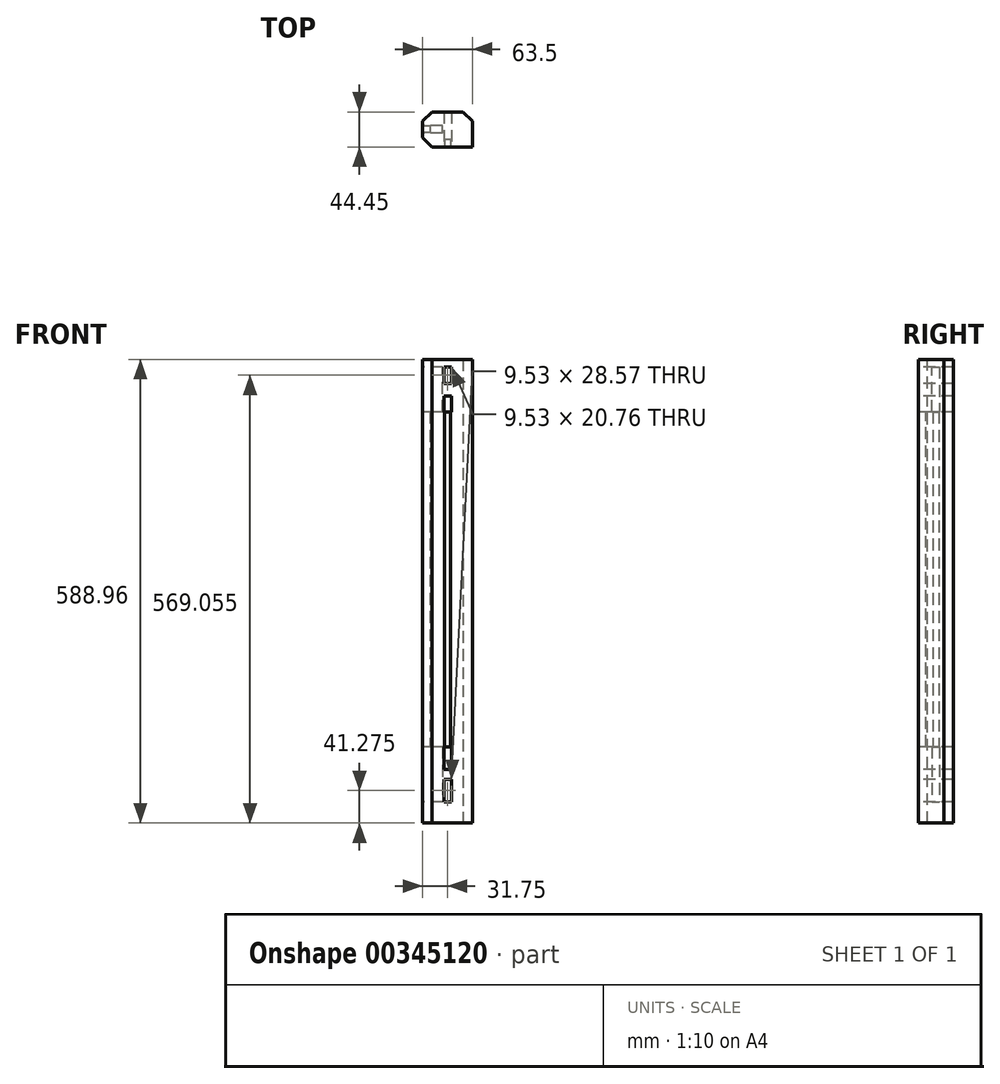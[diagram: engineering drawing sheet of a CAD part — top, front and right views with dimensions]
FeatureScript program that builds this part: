
annotation { "Feature Type Name" : "Feature", "Feature Type Description" : "" }
export const myFeature = defineFeature(function(context is Context, id is Id, definition is map)
    precondition{}
    {
        {
            var Q0;
            Q0=qCreatedBy(makeId("Top.planeOp"),FACE);
            var sketch = newSketch(context, id + "F0", { "sketchPlane" : qUnion([Q0])});
            skLineSegment(sketch, "E0", {"start": v(0, 0) * mm, "end": v(63.5, 0) * mm});
            skLineSegment(sketch, "E1", {"start": v(63.5, 0) * mm, "end": v(63.5, 44.45) * mm});
            skLineSegment(sketch, "E2", {"start": v(63.5, 44.45) * mm, "end": v(0, 44.45) * mm});
            skLineSegment(sketch, "E3", {"start": v(0, 44.45) * mm, "end": v(0, 0) * mm});
            skSolve(sketch);
        }
        {
            var Q0;
            Q0=qSketchRegion(id+"F0",true);
            extrude(context, id + "F1", {"entities" : qUnion([Q0]), "depth" : 588.96 * mm});
        }
        {
            var Q0;
            Q0=makeQuery(id+"F1.opExtrude","SWEPT_FACE",FACE,{"disambiguationData":[OSD([sQuery(id+"F0.wireOp",EDGE,"E3")])]});
            var sketch = newSketch(context, id + "F2", { "sketchPlane" : qUnion([Q0])});
            skLineSegment(sketch, "E4", {"start": v(-26.99, 579.44) * mm, "end": v(-26.99, 522.29) * mm});
            skLineSegment(sketch, "E5", {"start": v(-26.99, 522.29) * mm, "end": v(-17.46, 522.29) * mm});
            skLineSegment(sketch, "E6", {"start": v(-17.46, 522.29) * mm, "end": v(-17.46, 579.44) * mm});
            skLineSegment(sketch, "E7", {"start": v(-17.46, 579.44) * mm, "end": v(-26.99, 579.44) * mm});
            skPoint(sketch, "E8", {"position": v(-26.2, 522.29) * mm});
            skPoint(sketch, "E9", {"position": v(-18.26, 522.29) * mm});
            skLineSegment(sketch, "E10.bottom", {"start": v(-17.46, 96.84) * mm, "end": v(-26.99, 96.84) * mm});
            skLineSegment(sketch, "E10.top", {"start": v(-17.46, 26.99) * mm, "end": v(-26.99, 26.99) * mm});
            skLineSegment(sketch, "E10.left", {"start": v(-17.46, 96.84) * mm, "end": v(-17.46, 26.99) * mm});
            skLineSegment(sketch, "E10.right", {"start": v(-26.99, 96.84) * mm, "end": v(-26.99, 26.99) * mm});
            skPoint(sketch, "E10.middle", {"position": v(-22.23, 61.91) * mm});
            skPoint(sketch, "E10.middle.positionSnap0", {"position": v(-22.22, 0) * mm});
            skPoint(sketch, "E10.centerSnap0", {"position": v(-22.22, 0) * mm});
            skLineSegment(sketch, "E11", {"start": v(-18.26, 522.29) * mm, "end": v(-18.26, 96.84) * mm});
            skLineSegment(sketch, "E12", {"start": v(-26.2, 522.29) * mm, "end": v(-26.2, 96.84) * mm});
            skSolve(sketch);
        }
        {
            var Q0;
            {var subQ4=sQuery(id+"F2.wireOp",EDGE,"E4");Q0=makeQuery(id+"F2.imprint","IMPRINT",FACE,{"disambiguationData":[TD([[makeQuery(id+"F2.imprint","IMPRINT",EDGE,{"derivedFrom":subQ4}),1.0]])]});}
            var Q1;
            Q1=makeQuery(id+"F2.imprint","IMPRINT",FACE,{"disambiguationData":[TD([[makeQuery(id+"F2.imprint","IMPRINT",EDGE,{"derivedFrom":sQuery(id+"F2.wireOp",EDGE,"E10.top")}),-1.0]])]});
            extrude(context, id + "F3", {"entities" : qUnion([Q0, Q1]), "operationType" : NewBodyOperationType.REMOVE, "oppositeDirection" : true, "depth" : 25.4 * mm});
        }
        {
            var Q0;
            Q0 = qSketchRegion(id + "F2", true);
            extrude(context, id + "F4", {"entities" : qUnion([Q0]), "operationType" : NewBodyOperationType.REMOVE, "oppositeDirection" : true, "depth" : 9.52 * mm});
        }
        {
            var Q0;
            Q0=makeQuery(id+"F1.opExtrude","SWEPT_FACE",FACE,{"disambiguationData":[OSD([sQuery(id+"F0.wireOp",EDGE,"E0")])]});
            var sketch = newSketch(context, id + "F5", { "sketchPlane" : qUnion([Q0])});
            skLineSegment(sketch, "E13", {"start": v(26.99, 579.44) * mm, "end": v(26.99, 558.67) * mm});
            skLineSegment(sketch, "E14", {"start": v(26.99, 558.67) * mm, "end": v(36.51, 558.67) * mm});
            skLineSegment(sketch, "E15", {"start": v(36.51, 558.67) * mm, "end": v(36.51, 579.44) * mm});
            skLineSegment(sketch, "E16", {"start": v(36.51, 579.44) * mm, "end": v(26.99, 579.44) * mm});
            skPoint(sketch, "E17.startSnap0", {"position": v(26.99, 569.06) * mm});
            skLineSegment(sketch, "E18", {"start": v(26.99, 55.56) * mm, "end": v(36.51, 55.56) * mm});
            skLineSegment(sketch, "E19", {"start": v(28.78, 522.03) * mm, "end": v(26.99, 522.03) * mm});
            skLineSegment(sketch, "E20", {"start": v(26.99, 522.03) * mm, "end": v(26.99, 522.03) * mm});
            skLineSegment(sketch, "E21", {"start": v(26.99, 522.03) * mm, "end": v(26.99, 542.8) * mm});
            skLineSegment(sketch, "E22", {"start": v(26.99, 542.8) * mm, "end": v(36.51, 542.8) * mm});
            skLineSegment(sketch, "E23", {"start": v(36.51, 542.8) * mm, "end": v(36.51, 522.03) * mm});
            skLineSegment(sketch, "E24", {"start": v(36.51, 522.03) * mm, "end": v(28.78, 522.03) * mm});
            skLineSegment(sketch, "E25", {"start": v(26.99, 55.56) * mm, "end": v(26.99, 55.56) * mm});
            skLineSegment(sketch, "E26", {"start": v(26.99, 55.56) * mm, "end": v(26.99, 26.99) * mm});
            skLineSegment(sketch, "E27", {"start": v(36.51, 55.56) * mm, "end": v(36.51, 26.99) * mm});
            skLineSegment(sketch, "E28", {"start": v(36.51, 26.99) * mm, "end": v(26.99, 26.99) * mm});
            skLineSegment(sketch, "E29", {"start": v(36.51, 68.26) * mm, "end": v(36.51, 96.84) * mm});
            skLineSegment(sketch, "E30", {"start": v(36.51, 96.84) * mm, "end": v(26.99, 96.84) * mm});
            skLineSegment(sketch, "E31", {"start": v(26.99, 96.84) * mm, "end": v(26.99, 68.26) * mm});
            skLineSegment(sketch, "E32", {"start": v(26.99, 68.26) * mm, "end": v(36.51, 68.26) * mm});
            skPoint(sketch, "E33", {"position": v(35.82, 96.84) * mm});
            skPoint(sketch, "E34", {"position": v(27.88, 96.84) * mm});
            skLineSegment(sketch, "E35", {"start": v(35.82, 96.84) * mm, "end": v(35.82, 522.03) * mm});
            skLineSegment(sketch, "E36", {"start": v(27.88, 96.84) * mm, "end": v(27.88, 522.03) * mm});
            skSolve(sketch);
        }
        {
            var Q0;
            {var subQ0=sQuery(id+"F5.wireOp",EDGE,"E35");Q0=makeQuery(id+"F5.imprint","IMPRINT",FACE,{"disambiguationData":[TD([[makeQuery(id+"F5.imprint","IMPRINT",EDGE,{"derivedFrom":subQ0}),1.0]])]});}
            extrude(context, id + "F6", {"entities" : qUnion([Q0]), "operationType" : NewBodyOperationType.REMOVE, "oppositeDirection" : true, "depth" : 9.52 * mm});
        }
        {
            var Q0;
            Q0=makeQuery(id+"F5.imprint","IMPRINT",FACE,{"disambiguationData":[TD([[makeQuery(id+"F5.imprint","IMPRINT",EDGE,{"derivedFrom":sQuery(id+"F5.wireOp",EDGE,"E13")}),1.0]])]});
            var Q1;
            {var subQ0=sQuery(id+"F5.wireOp",EDGE,"E21");Q1=makeQuery(id+"F5.imprint","IMPRINT",FACE,{"disambiguationData":[TD([[makeQuery(id+"F5.imprint","IMPRINT",EDGE,{"derivedFrom":subQ0}),-1.0]])]});}
            var Q2;
            {var subQ4=sQuery(id+"F5.wireOp",EDGE,"E29");Q2=makeQuery(id+"F5.imprint","IMPRINT",FACE,{"disambiguationData":[TD([[makeQuery(id+"F5.imprint","IMPRINT",EDGE,{"derivedFrom":subQ4}),1.0]])]});}
            var Q3;
            Q3=makeQuery(id+"F5.imprint","IMPRINT",FACE,{"disambiguationData":[TD([[makeQuery(id+"F5.imprint","IMPRINT",EDGE,{"derivedFrom":sQuery(id+"F5.wireOp",EDGE,"E18")}),-1.0]])]});
            extrude(context, id + "F7", {"entities" : qUnion([Q0, Q1, Q2, Q3]), "operationType" : NewBodyOperationType.REMOVE, "endBound" : BoundingType.THROUGH_ALL, "oppositeDirection" : true, "depth" : 25.4 * mm});
        }
        {
            var Q0;
            Q0=makeQuery(id+"F1.opExtrude","SWEPT_EDGE",EDGE,{"disambiguationData":[OSD([sQuery(id+"F0.wireOp",EDGE,"E1"),sQuery(id+"F0.wireOp",EDGE,"E2")])]});
            var Q1;
            Q1=makeQuery(id+"F1.opExtrude","SWEPT_EDGE",EDGE,{"disambiguationData":[OSD([sQuery(id+"F0.wireOp",EDGE,"E2"),sQuery(id+"F0.wireOp",EDGE,"E3")])]});
            var Q2;
            Q2=makeQuery(id+"F1.opExtrude","SWEPT_EDGE",EDGE,{"disambiguationData":[OSD([sQuery(id+"F0.wireOp",EDGE,"E0"),sQuery(id+"F0.wireOp",EDGE,"E3")])]});
            chamfer(context, id + "F8", {"entities" : qUnion([Q0, Q1, Q2]), "width" : 11.9 * mm, "tangentPropagation" : true});
        }
    });
